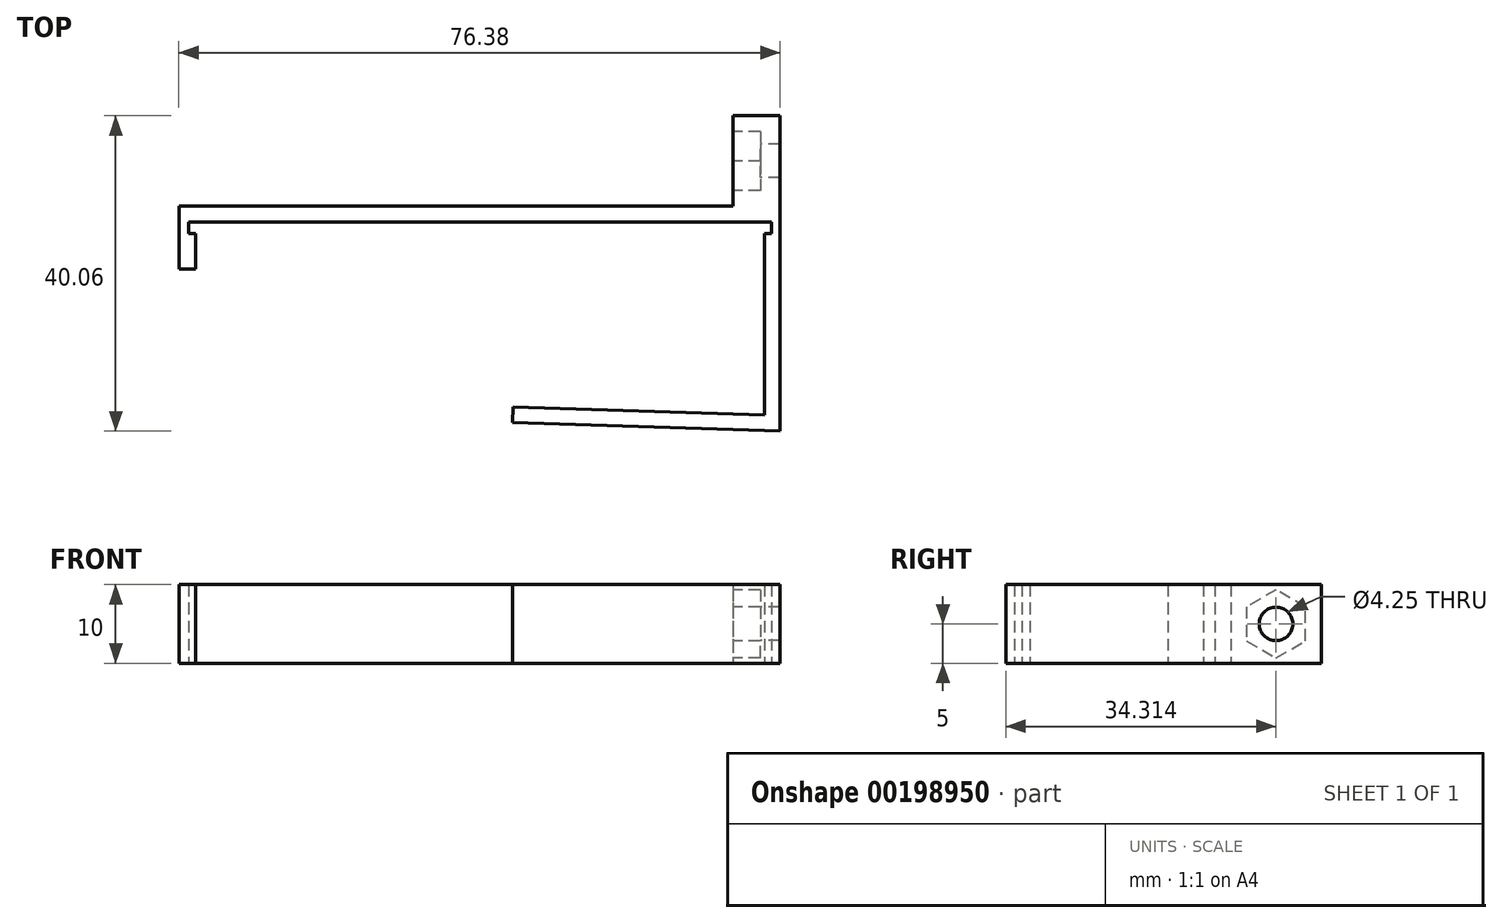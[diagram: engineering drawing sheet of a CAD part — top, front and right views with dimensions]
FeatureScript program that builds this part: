
annotation { "Feature Type Name" : "Feature", "Feature Type Description" : "" }
export const myFeature = defineFeature(function(context is Context, id is Id, definition is map)
    precondition{}
    {
        {
            var Q0;
            Q0=qCreatedBy(makeId("Top.planeOp"),FACE);
            var sketch = newSketch(context, id + "F0", { "sketchPlane" : qUnion([Q0])});
            skLineSegment(sketch, "E0", {"start": v(-1.12, 26.56) * mm, "end": v(-75.12, 26.56) * mm});
            skLineSegment(sketch, "E1", {"start": v(-74.25, 20.56) * mm, "end": v(-76.38, 20.56) * mm});
            skLineSegment(sketch, "E2", {"start": v(-76.38, 20.56) * mm, "end": v(-76.38, 28.56) * mm});
            skLineSegment(sketch, "E3", {"start": v(-76.38, 28.56) * mm, "end": v(-6, 28.56) * mm});
            skLineSegment(sketch, "E4", {"start": v(-6, 28.56) * mm, "end": v(-6, 40.06) * mm});
            skLineSegment(sketch, "E5", {"start": v(-6, 40.06) * mm, "end": v(0, 40.06) * mm});
            skLineSegment(sketch, "E6", {"start": v(0, 40.06) * mm, "end": v(0, 0) * mm});
            skLineSegment(sketch, "E7", {"start": v(0, 0) * mm, "end": v(-34, 1.06) * mm});
            skLineSegment(sketch, "E8", {"start": v(-34, 1.06) * mm, "end": v(-33.94, 3.06) * mm});
            skLineSegment(sketch, "E9", {"start": v(-33.94, 3.06) * mm, "end": v(-2, 2.06) * mm});
            skLineSegment(sketch, "E10", {"start": v(-75.12, 26.56) * mm, "end": v(-75.12, 25.06) * mm});
            skLineSegment(sketch, "E11", {"start": v(-75.12, 25.06) * mm, "end": v(-74.25, 25.06) * mm});
            skLineSegment(sketch, "E12", {"start": v(-74.25, 25.06) * mm, "end": v(-74.25, 20.56) * mm});
            skLineSegment(sketch, "E13", {"start": v(-1.12, 26.56) * mm, "end": v(-1.12, 25.06) * mm});
            skLineSegment(sketch, "E14", {"start": v(-1.12, 25.06) * mm, "end": v(-2, 25.06) * mm});
            skLineSegment(sketch, "E15", {"start": v(-2, 25.06) * mm, "end": v(-2, 2.06) * mm});
            skSolve(sketch);
        }
        {
            var Q0;
            Q0 = qSketchRegion(id + "F0", true);
            extrude(context, id + "F1", {"entities" : qUnion([Q0]), "depth" : 10 * mm});
        }
        {
            var Q0;
            Q0=makeQuery(id+"F1.opExtrude","SWEPT_FACE",FACE,{"disambiguationData":[OSD([sQuery(id+"F0.wireOp",EDGE,"E4")])]});
            var sketch = newSketch(context, id + "F2", { "sketchPlane" : qUnion([Q0])});
            skCircle(sketch, "E16.cCircle", {"center": v(-34.31, 5) * mm, "radius": 3.75 * mm, "construction": true});
            skLineSegment(sketch, "E16.0", {"start": v(-30.56, 7.17) * mm, "end": v(-30.56, 2.83) * mm});
            skLineSegment(sketch, "E16.1", {"start": v(-30.56, 2.83) * mm, "end": v(-34.31, 0.67) * mm});
            skLineSegment(sketch, "E16.2", {"start": v(-34.31, 0.67) * mm, "end": v(-38.06, 2.83) * mm});
            skLineSegment(sketch, "E16.3", {"start": v(-38.06, 2.83) * mm, "end": v(-38.06, 7.17) * mm});
            skLineSegment(sketch, "E16.4", {"start": v(-38.06, 7.17) * mm, "end": v(-34.31, 9.33) * mm});
            skLineSegment(sketch, "E16.5", {"start": v(-34.31, 9.33) * mm, "end": v(-30.56, 7.17) * mm});
            skPoint(sketch, "E16.0.midPoint", {"position": v(-30.56, 5) * mm});
            skPoint(sketch, "E17", {"position": v(-40.06, 5) * mm});
            skPoint(sketch, "E18", {"position": v(-34.31, 10) * mm});
            skSolve(sketch);
        }
        {
            var Q0;
            Q0 = qSketchRegion(id + "F2", true);
            extrude(context, id + "F3", {"entities" : qUnion([Q0]), "operationType" : NewBodyOperationType.REMOVE, "oppositeDirection" : true, "depth" : 3.5 * mm});
        }
        {
            var Q0;
            Q0=makeQuery(id+"F3.boolean.opBoolean","COPY",FACE,{"derivedFrom":makeQuery(id+"F3.opExtrude","CAP_FACE",FACE,{"disambiguationData":[OSD([sQuery(id+"F2.wireOp",EDGE,"E16.0"),sQuery(id+"F2.wireOp",EDGE,"E16.1"),sQuery(id+"F2.wireOp",EDGE,"E16.2"),sQuery(id+"F2.wireOp",EDGE,"E16.3"),sQuery(id+"F2.wireOp",EDGE,"E16.4"),sQuery(id+"F2.wireOp",EDGE,"E16.5")])],"isStart":false})});
            var sketch = newSketch(context, id + "F4", { "sketchPlane" : qUnion([Q0])});
            skCircle(sketch, "E19", {"center": v(-34.31, 5) * mm, "radius": 2.12 * mm});
            skSolve(sketch);
        }
        {
            var Q0;
            Q0 = qSketchRegion(id + "F4", true);
            extrude(context, id + "F5", {"entities" : qUnion([Q0]), "operationType" : NewBodyOperationType.REMOVE, "endBound" : BoundingType.UP_TO_NEXT, "oppositeDirection" : true, "depth" : 25 * mm});
        }
    });
